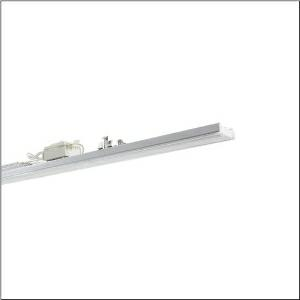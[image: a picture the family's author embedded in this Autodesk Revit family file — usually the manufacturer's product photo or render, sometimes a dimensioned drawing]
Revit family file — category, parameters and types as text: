
# Revit family: licross_r__21_recessed_mo_52tl1edn455g_4166
name_source: partatom
category: Lighting Fixtures
units: mm (PartAtom-declared; Revit-internal decimal feet)

## family parameters
Cut with Voids When Loaded = No
Host = Face
Light Source = No
Part Type = Normal
Room Calculation Point = No
Round Connector Dimension = Use Diameter
Shared = No

## types (1)
- --- (1 x LED, 5800 lm, 32.4 W, 4000K)
    Apparent Load = 32 VA
    CIE Flux Codes = 85 95 99 100 100
    Color Rendering = 80
    Color Temperature = 4000K
    Default Elevation = 1800 mm
    Description = Licross® 21 Recessed MO, luminaire insert, of sheet steel, galvanised, coil coated, white, length: 1.500mm, width: 66mm, height: 67mm, LED rated luminous flux: 5.800lm, light colour: 840, control gear: DALI 2, with plug, 5-pole, with phase selection, mains connection: 220..240V, AC, 50/60Hz, rated input power: 32W, internal wiring halogen-free, primary light control with lens, of plastic, primary optical cover: cover, of PMMA, light emission: direct distribution, primary light characteristic: symmetric, protection rating (complete): IP40, insulation class (complete): insulation class I (protective earthing), certification: CE, ENEC, VDE, UKCA, protection symbol: D if used in an environment without relevant dust loads with corresponding accessories, impact resistance: IK06, permissible ambient temperature for indoor applications: -25..+45°C, corresponds to IFS (International Featured Standards) requirements for safety and quality in the food industry, reducing of maximum allowable ambient temperature of 5°C with ceiling mounting, LABS conformity tested according to VDMA 24364:2018-05, packaging unit: 1 piece
    Height = 58 mm
    Lamp = 1 x LED
    Lamp Light Flux = 5800 lm
    Lamp Power = 32.4 W
    Lamp count = 1
    Length = 1500 mm
    Luminous efficacy = 179 lm/W
    Manufacturer = Siteco
    ModVariant = No
    Model = 52TL1EDN455G
    Mounting Place = Ceiling
    Mounting Type = Pendant
    Number of Poles = 1
    OnlyDefault = Yes
    Power Factor = 1
    Product Name = Licross® 21 Recessed MO
    Product group = luminaire insert | ceiling pendant
    ProductGroupID = 902
    Protection Class = Protection class I
    Protection Degree = IP 40
    RLX_Detail_Level = 1
    RLX_Emergency_Light_Flux = 0 lm
    RLX_Emergency_Type = 0
    RLX_Emergency_Type_DB = No
    RlxData = <blob elided: 24373 chars, md5=5da0f6b8>
    Socket = socket
    Standby Power = 0 W
    System Light Flux = 5800 lm
    System Power = 32 W
    Type Comments = factory setting: luminous flux: 100 % | dim-lin: 254 | 219 mA
    Type Image = l_1296930.jpg
    URL = http://relux.com
    VarID = @adj_146825
    Voltage = 0 V
    Weight = 0.00 kg
    Width = 66 mm

## geometry (parser evidence)
native form markers: Blend x4, Sweep x9
no freeform markers — native parametric forms only
